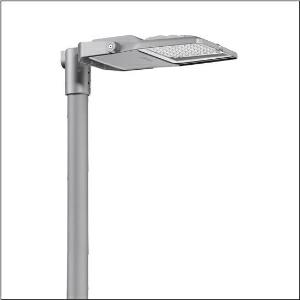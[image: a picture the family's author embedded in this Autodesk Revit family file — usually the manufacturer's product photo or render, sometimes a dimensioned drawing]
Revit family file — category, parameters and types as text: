
# Revit family: floodlight_fl_21_mini___pl52_5xa7775c2d3a_b3eb
name_source: partatom
category: Lighting Fixtures
units: mm (PartAtom-declared; Revit-internal decimal feet)

## family parameters
Cut with Voids When Loaded = No
Host = Face
Light Source = No
Part Type = Normal
Room Calculation Point = No
Round Connector Dimension = Use Diameter
Shared = No

## types (1)
- --- (1 x LED, 12190 lm, 89 W, 3000K)
    Apparent Load = 89 VA
    CIE Flux Codes = 26 60 98 100 100
    Color Rendering = 70
    Color Temperature = 3000K
    Default Elevation = 1800 mm
    Description = Floodlight FL 21 mini, floodlight, primary light control with lens, of PMMA, primary optical cover: protective disc, of toughened safety glass, transparent, light distribution: PL52, light emission: direct distribution, installation type: surface-mounted, LED, High Power LED, rated luminous flux: 12.190lm, luminous efficacy: 137lm/W, light colour: 730, colour temperature: 3000K, control: flexible luminous flux parameterisation, time-dependent luminous flux control, constant luminous flux control, overheat protection, presetting dimming logarithmic, with terminal, 6-pole, mains connection: 220..240V, AC, 50/60Hz, start of lifetime: 89W, end of service life: 94W, reduction: 43W, luminaire housing, of diecast aluminium, powder-coated, Siteco® metallic grey (DB 702S), corrosivity category C5 mid according to DIN EN ISO 12944, sealing non-destructively replaceable, please order mast flange separately, mast bracket, of steel, galvanised, powder-coated, Siteco® metallic grey (DB 702S), Smart Interface above, protection rating (complete): IP66, insulation class (complete): insulation class II (safety insulation), certification: CE, ENEC, VDE, protection symbol: D, impact resistance: IK08, permissible operating ambient temperature: -40..+40°C, permissible operating ambient temperature for outdoor applications: -40..+50°C, standard: DIN EN 12944, LABS conformity tested according to VDMA 24364:2018-05, packaging unit: 1 piece

Light Distribution: PL52
    Height = 70 mm
    Lamp = 1 x LED
    Lamp Light Flux = 12190 lm
    Lamp Power = 89 W
    Lamp count = 1
    Length = 485 mm
    Luminous efficacy = 137 lm/W
    Manufacturer = Siteco
    ModVariant = No
    Model = 5XA7775C2D3A
    Number of Poles = 1
    OnlyDefault = Yes
    Power Factor = 1
    Product Name = Floodlight FL 21 mini | PL52
    Product group = floodlight | pylon annexe
    ProductGroupID = 6200
    Protection Class = Protection class II
    Protection Degree = IP 66
    RLX_Detail_Level = 1
    RLX_Emergency_Light_Flux = 0 lm
    RLX_Emergency_Type = 0
    RLX_Emergency_Type_DB = No
    RlxData = <blob elided: 101033 chars, md5=b544bcc7>
    Socket = socket
    Standby Power = 0 W
    System Light Flux = 12190 lm
    System Power = 89 W
    Type Comments = factory setting: luminous flux: 100 % | dim-lin: 254 | 456 mA
    Type Image = l_1007125.jpg
    URL = http://relux.com
    VarID = @adj_095621
    Voltage = 0 V
    Weight = 0.00 kg
    Width = 337 mm

## geometry (parser evidence)
native form markers: Blend x4, Sweep x12
no freeform markers — native parametric forms only
